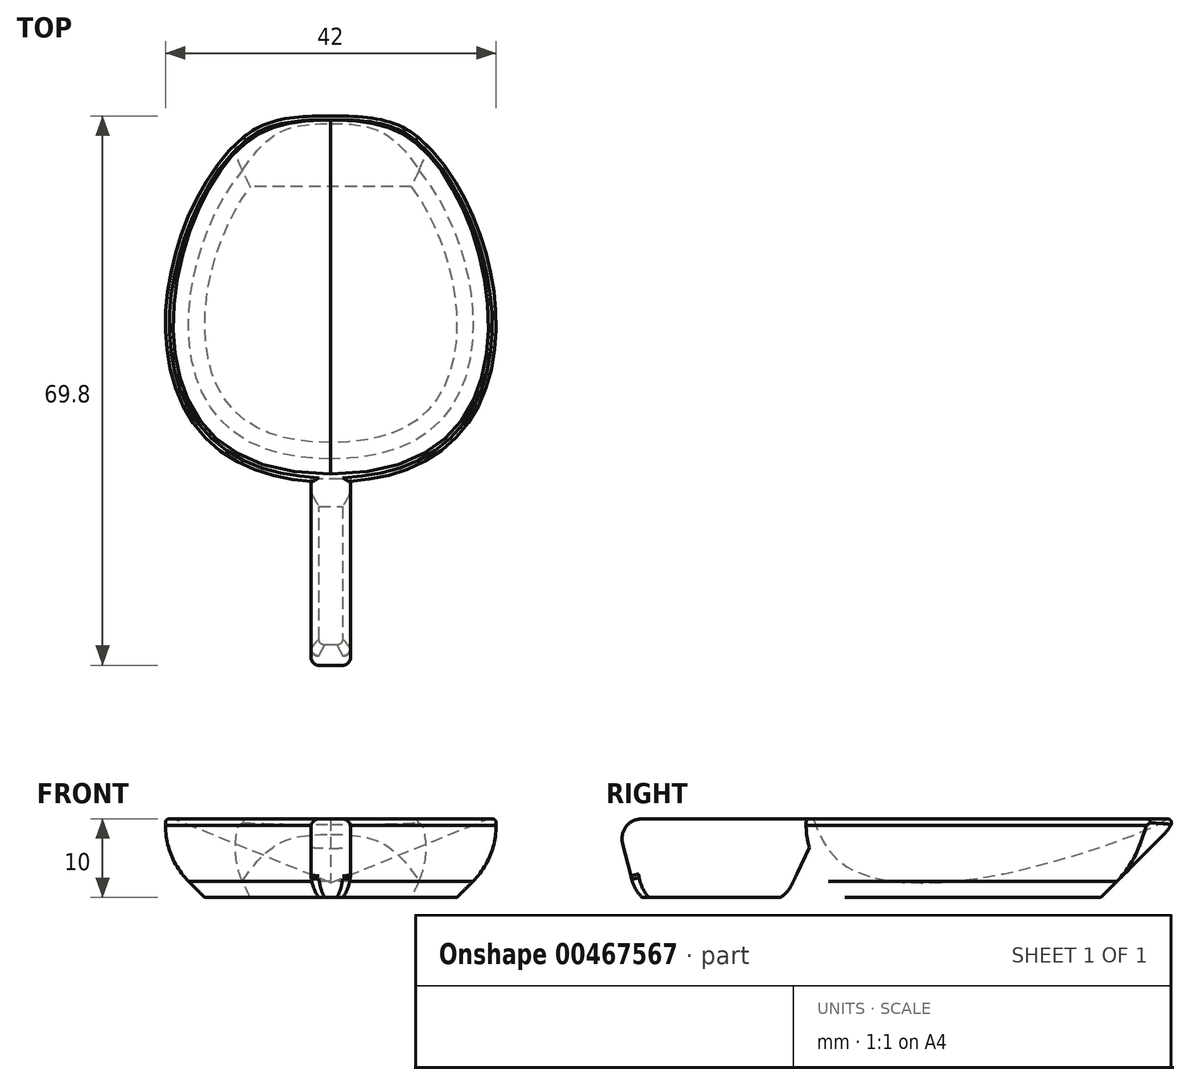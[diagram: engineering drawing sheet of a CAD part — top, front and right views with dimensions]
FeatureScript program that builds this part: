
annotation { "Feature Type Name" : "Feature", "Feature Type Description" : "" }
export const myFeature = defineFeature(function(context is Context, id is Id, definition is map)
    precondition{}
    {
        {
            var Q0;
            Q0=qCreatedBy(makeId("Top.planeOp"),FACE);
            var sketch = newSketch(context, id + "F0", { "sketchPlane" : qUnion([Q0])});
            skFitSpline(sketch, "E0", {"points": [v(0, 45) * mm, v(-12, 41) * mm, v(-20, 18) * mm, v(0, 0) * mm], "startDerivative": vector(-57.69, 0) * mm, "endDerivative": vector(118.66, 0) * mm});
            skLineSegment(sketch, "E1", {"start": v(0, 45) * mm, "end": v(0, 0) * mm});
            skSolve(sketch);
        }
        {
            var Q0;
            Q0=qCreatedBy(makeId("Right.planeOp"),FACE);
            var sketch = newSketch(context, id + "F1", { "sketchPlane" : qUnion([Q0])});
            skLineSegment(sketch, "E2", {"start": v(0, 0) * mm, "end": v(45, 0) * mm});
            skFitSpline(sketch, "E3", {"points": [v(0, 0) * mm, v(5, -6.5) * mm, v(24, -7) * mm, v(45, 0) * mm], "startDerivative": vector(12.5, -37.49) * mm, "endDerivative": vector(15.21, 11.4) * mm});
            skSolve(sketch);
        }
        {
            var Q0;
            Q0 = qSketchRegion(id + "F1", true);
            var Q1;
            Q1 = qSketchRegion(id + "F0", true);
            var Q2;
            Q2=sQuery(id+"FQMcYZS5QZvl0eC_1.wireOp",EDGE,"xzcCkyq8-KsDK-qB1P-N4Ot-IK7GxVPd1evt");
            loft(context, id + "F2", {"sheetProfilesArray" : [{ "sheetProfileEntities" : qUnion([Q0]) }, { "sheetProfileEntities" : qUnion([Q1]) }], "guidesArray" : [{ "guideEntities" : qUnion([Q2]), "guideDerivativeType" : LoftGuideDerivativeType.DEFAULT, "guideDerivativeMagnitude" : 1 }]});
        }
        {
            var Q0;
            Q0=makeQuery(id+"F2.opLoft","SWEPT_BODY",BODY,{"disambiguationData":[OSD([makeQuery(id+"F0.imprint","IMPRINT",FACE,{"disambiguationData":[TD([[makeQuery(id+"F0.imprint","IMPRINT",EDGE,{"derivedFrom":sQuery(id+"F0.wireOp",EDGE,"E0")}),1.0]])]}),makeQuery(id+"F1.imprint","IMPRINT",FACE,{"disambiguationData":[TD([[makeQuery(id+"F1.imprint","IMPRINT",EDGE,{"derivedFrom":sQuery(id+"F1.wireOp",EDGE,"C926cNkA-Lv8C-HaRY-GubS-DPcHZd8qW3n6")}),1.0]])]})])]});
            var Q1;
            Q1=qCreatedBy(makeId("Right.planeOp"),FACE);
            mirror(context, id + "F3", {"operationType" : NewBodyOperationType.ADD, "entities" : qUnion([Q0]), "mirrorPlane" : qUnion([Q1])});
        }
        {
            var Q0;
            Q0=qCreatedBy(makeId("Top.planeOp"),FACE);
            var sketch = newSketch(context, id + "F4", { "sketchPlane" : qUnion([Q0])});
            skFitSpline(sketch, "E4", {"points": [v(0, 46) * mm, v(-12, 42) * mm, v(-21, 19) * mm, v(0, -1) * mm], "startDerivative": vector(-58.67, 0) * mm, "endDerivative": vector(124, 0) * mm});
            skLineSegment(sketch, "E5", {"start": v(0, 46) * mm, "end": v(0, -1) * mm});
            skSolve(sketch);
        }
        {
            var Q0;
            Q0 = qSketchRegion(id + "F4", true);
            extrude(context, id + "F5", {"entities" : qUnion([Q0]), "oppositeDirection" : true, "depth" : 10 * mm});
        }
        {
            var Q0;
            Q0=makeQuery(id+"F2.opLoft","SWEPT_BODY",BODY,{"disambiguationData":[OSD([makeQuery(id+"F0.imprint","IMPRINT",FACE,{"disambiguationData":[TD([[makeQuery(id+"F0.imprint","IMPRINT",EDGE,{"derivedFrom":sQuery(id+"F0.wireOp",EDGE,"E0")}),1.0]])]}),makeQuery(id+"F1.imprint","IMPRINT",FACE,{"disambiguationData":[TD([[makeQuery(id+"F1.imprint","IMPRINT",EDGE,{"derivedFrom":sQuery(id+"F1.wireOp",EDGE,"C926cNkA-Lv8C-HaRY-GubS-DPcHZd8qW3n6")}),1.0]])]})])]});
            var Q1;
            Q1=makeQuery(id+"F5.opExtrude","SWEPT_BODY",BODY,{"disambiguationData":[OSD([sQuery(id+"F4.wireOp",EDGE,"E4"),sQuery(id+"F4.wireOp",EDGE,"E5")])]});
            booleanBodies(context, id + "F6", {"operationType" : BooleanOperationType.SUBTRACTION, "tools" : qUnion([Q0]), "targets" : qUnion([Q1])});
        }
        {
            var Q0;
            Q0=makeQuery(id+"F5.opExtrude","SWEPT_BODY",BODY,{"disambiguationData":[OSD([sQuery(id+"F4.wireOp",EDGE,"E4"),sQuery(id+"F4.wireOp",EDGE,"E5")])]});
            var Q1;
            Q1=qCreatedBy(makeId("Right.planeOp"),FACE);
            mirror(context, id + "F7", {"operationType" : NewBodyOperationType.ADD, "entities" : qUnion([Q0]), "mirrorPlane" : qUnion([Q1])});
        }
        {
            var Q0;
            Q0=qCreatedBy(makeId("Right.planeOp"),FACE);
            var sketch = newSketch(context, id + "F8", { "sketchPlane" : qUnion([Q0])});
            skLineSegment(sketch, "E6", {"start": v(0, 0) * mm, "end": v(-25, 0) * mm});
            skLineSegment(sketch, "E7", {"start": v(-25, 0) * mm, "end": v(-22.5, -10) * mm});
            skLineSegment(sketch, "E8", {"start": v(-22.5, -10) * mm, "end": v(-3.5, -10) * mm});
            skLineSegment(sketch, "E9", {"start": v(-3.5, -10) * mm, "end": v(0, -2.5) * mm});
            skLineSegment(sketch, "E10", {"start": v(0, -2.5) * mm, "end": v(0, -2.5) * mm});
            skLineSegment(sketch, "E11", {"start": v(0, -2.5) * mm, "end": v(0, 0) * mm});
            skSolve(sketch);
        }
        {
            var Q0;
            Q0 = qSketchRegion(id + "F8", true);
            extrude(context, id + "F9", {"entities" : qUnion([Q0]), "operationType" : NewBodyOperationType.ADD, "endBound" : BoundingType.SYMMETRIC, "depth" : 5 * mm});
        }
        {
            var Q0;
            Q0=qCreatedBy(makeId("Right.planeOp"),FACE);
            var sketch = newSketch(context, id + "F10", { "sketchPlane" : qUnion([Q0])});
            skLineSegment(sketch, "E12", {"start": v(46.5, 0) * mm, "end": v(31.5, -15) * mm});
            skLineSegment(sketch, "E13", {"start": v(31.5, -15) * mm, "end": v(46.5, -15) * mm});
            skLineSegment(sketch, "E14", {"start": v(46.5, -15) * mm, "end": v(46.5, 0) * mm});
            skSolve(sketch);
        }
        {
            var Q0;
            Q0 = qSketchRegion(id + "F10", true);
            extrude(context, id + "F11", {"entities" : qUnion([Q0]), "operationType" : NewBodyOperationType.REMOVE, "endBound" : BoundingType.SYMMETRIC, "depth" : 25 * mm});
        }
        {
            var Q0;
            Q0=makeQuery(id+"F11.boolean.opBoolean","INTERSECT",EDGE,{"derivedFrom":[makeQuery(id+"F5.opExtrude","SWEPT_FACE",FACE,{"disambiguationData":[OSD([sQuery(id+"F4.wireOp",EDGE,"E4")])]}),makeQuery(id+"F11.opExtrude","SWEPT_FACE",FACE,{"disambiguationData":[OSD([sQuery(id+"F10.wireOp",EDGE,"E12")])]})]});
            var Q1;
            Q1=makeQuery(id+"F11.boolean.opBoolean","INTERSECT",EDGE,{"derivedFrom":[makeQuery(id+"F7.opPattern","COPY",FACE,{"derivedFrom":makeQuery(id+"F5.opExtrude","SWEPT_FACE",FACE,{"disambiguationData":[OSD([sQuery(id+"F4.wireOp",EDGE,"E4")])]}),"instanceName":"1"}),makeQuery(id+"F11.opExtrude","SWEPT_FACE",FACE,{"disambiguationData":[OSD([sQuery(id+"F10.wireOp",EDGE,"E12")])]})]});
            fillet(context, id + "F12", {"entities" : qUnion([Q0, Q1]), "radius" : 5 * mm, "tangentPropagation" : true, "allowEdgeOverflow" : false});
        }
        {
            var Q0;
            Q0=makeQuery(id+"F7.opPattern","COPY",EDGE,{"derivedFrom":makeQuery(id+"F5.opExtrude","CAP_EDGE",EDGE,{"disambiguationData":[OSD([sQuery(id+"F4.wireOp",EDGE,"E4")])],"isStart":false}),"instanceName":"1"});
            chamfer(context, id + "F13", {"entities" : qUnion([Q0]), "width" : 5 * mm, "tangentPropagation" : true});
        }
        {
            var Q0;
            Q0=makeQuery(id+"F9.opExtrude","SWEPT_FACE",FACE,{"disambiguationData":[OSD([sQuery(id+"F8.wireOp",EDGE,"E8")])]});
            chamfer(context, id + "F14", {"entities" : qUnion([Q0]), "width" : 1 * mm, "tangentPropagation" : true});
        }
        {
            var Q0;
            {var subQ0=sQuery(id+"F8.wireOp",EDGE,"E9");Q0=makeQuery(id+"F14.opChamfer","BLEND_EDGE",EDGE,{"blendedFrom":[makeQuery(id+"F9.opExtrude","SWEPT_EDGE",EDGE,{"disambiguationData":[OSD([sQuery(id+"F8.wireOp",EDGE,"E8"),subQ0])]}),makeQuery(id+"F9.opExtrude","SWEPT_FACE",FACE,{"disambiguationData":[OSD([subQ0])]})],"blendedInto":[makeQuery(id+"F9.opExtrude","SWEPT_FACE",FACE,{"disambiguationData":[OSD([subQ0])]})]});}
            var Q1;
            {var subQ0=sQuery(id+"F8.wireOp",EDGE,"E8");Q1=makeQuery(id+"F14.opChamfer","BLEND_EDGE",EDGE,{"blendedFrom":[makeQuery(id+"F9.opExtrude","CAP_EDGE",EDGE,{"disambiguationData":[OSD([subQ0])],"isStart":true}),makeQuery(id+"F9.opExtrude","CAP_FACE",FACE,{"disambiguationData":[OSD([sQuery(id+"F8.wireOp",EDGE,"E6"),sQuery(id+"F8.wireOp",EDGE,"E7"),subQ0,sQuery(id+"F8.wireOp",EDGE,"E9"),sQuery(id+"F8.wireOp",EDGE,"E11")])],"isStart":true})],"blendedInto":[makeQuery(id+"F9.opExtrude","CAP_FACE",FACE,{"disambiguationData":[OSD([sQuery(id+"F8.wireOp",EDGE,"E6"),sQuery(id+"F8.wireOp",EDGE,"E7"),subQ0,sQuery(id+"F8.wireOp",EDGE,"E9"),sQuery(id+"F8.wireOp",EDGE,"E11")])],"isStart":true})]});}
            var Q2;
            {var subQ0=sQuery(id+"F8.wireOp",EDGE,"E7");Q2=makeQuery(id+"F14.opChamfer","BLEND_EDGE",EDGE,{"blendedFrom":[makeQuery(id+"F9.opExtrude","SWEPT_EDGE",EDGE,{"disambiguationData":[OSD([subQ0,sQuery(id+"F8.wireOp",EDGE,"E8")])]}),makeQuery(id+"F9.opExtrude","SWEPT_FACE",FACE,{"disambiguationData":[OSD([subQ0])]})],"blendedInto":[makeQuery(id+"F9.opExtrude","SWEPT_FACE",FACE,{"disambiguationData":[OSD([subQ0])]})]});}
            var Q3;
            {var subQ0=sQuery(id+"F8.wireOp",EDGE,"E8");Q3=makeQuery(id+"F14.opChamfer","BLEND_EDGE",EDGE,{"blendedFrom":[makeQuery(id+"F9.opExtrude","CAP_EDGE",EDGE,{"disambiguationData":[OSD([subQ0])],"isStart":false}),makeQuery(id+"F9.opExtrude","CAP_FACE",FACE,{"disambiguationData":[OSD([sQuery(id+"F8.wireOp",EDGE,"E6"),sQuery(id+"F8.wireOp",EDGE,"E7"),subQ0,sQuery(id+"F8.wireOp",EDGE,"E9"),sQuery(id+"F8.wireOp",EDGE,"E11")])],"isStart":false})],"blendedInto":[makeQuery(id+"F9.opExtrude","CAP_FACE",FACE,{"disambiguationData":[OSD([sQuery(id+"F8.wireOp",EDGE,"E6"),sQuery(id+"F8.wireOp",EDGE,"E7"),subQ0,sQuery(id+"F8.wireOp",EDGE,"E9"),sQuery(id+"F8.wireOp",EDGE,"E11")])],"isStart":false})]});}
            fillet(context, id + "F15", {"entities" : qUnion([Q0, Q1, Q2, Q3]), "radius" : 5 * mm, "tangentPropagation" : true, "allowEdgeOverflow" : false});
        }
        {
            var Q0;
            Q0=makeQuery(id+"F9.opExtrude","SWEPT_EDGE",EDGE,{"disambiguationData":[OSD([sQuery(id+"F8.wireOp",EDGE,"E6"),sQuery(id+"F8.wireOp",EDGE,"E7")])]});
            fillet(context, id + "F16", {"entities" : qUnion([Q0]), "radius" : 2.5 * mm, "tangentPropagation" : true, "allowEdgeOverflow" : false});
        }
        {
            var Q0;
            Q0=makeQuery(id+"F9.opExtrude","CAP_EDGE",EDGE,{"disambiguationData":[OSD([sQuery(id+"F8.wireOp",EDGE,"E6")])],"isStart":true});
            var Q1;
            Q1=makeQuery(id+"F9.opExtrude","CAP_EDGE",EDGE,{"disambiguationData":[OSD([sQuery(id+"F8.wireOp",EDGE,"E6")])],"isStart":false});
            fillet(context, id + "F17", {"entities" : qUnion([Q0, Q1]), "radius" : 1 * mm, "tangentPropagation" : true, "allowEdgeOverflow" : false});
        }
        {
            var Q0;
            Q0=makeQuery(id+"F5.opExtrude","CAP_EDGE",EDGE,{"disambiguationData":[OSD([sQuery(id+"F4.wireOp",EDGE,"E4")])],"isStart":true});
            var Q1;
            Q1=makeQuery(id+"F6.opBoolean","COPY",EDGE,{"derivedFrom":makeQuery(id+"F2.opLoft","MID_CAP_EDGE",EDGE,{"disambiguationData":[OSD([sQuery(id+"F0.wireOp",EDGE,"E0"),sQuery(id+"F0.wireOp",EDGE,"E1")])],"capPos":1.0})});
            fillet(context, id + "F18", {"entities" : qUnion([Q0, Q1]), "radius" : 0.5 * mm, "tangentPropagation" : true, "allowEdgeOverflow" : false});
        }
        {
            var Q0;
            {var subQ0=sQuery(id+"F4.wireOp",EDGE,"E4");Q0=makeQuery(id+"F13.opChamfer","BLEND_EDGE",EDGE,{"blendedFrom":[makeQuery(id+"F7.opPattern","COPY",EDGE,{"derivedFrom":makeQuery(id+"F5.opExtrude","CAP_EDGE",EDGE,{"disambiguationData":[OSD([subQ0])],"isStart":false}),"instanceName":"1"}),makeQuery(id+"F7.opPattern","COPY",FACE,{"derivedFrom":makeQuery(id+"F5.opExtrude","SWEPT_FACE",FACE,{"disambiguationData":[OSD([subQ0])]}),"instanceName":"1"})],"blendedInto":[makeQuery(id+"F7.opPattern","COPY",FACE,{"derivedFrom":makeQuery(id+"F5.opExtrude","SWEPT_FACE",FACE,{"disambiguationData":[OSD([subQ0])]}),"instanceName":"1"})]});}
            fillet(context, id + "F19", {"entities" : qUnion([Q0]), "radius" : 10 * mm, "tangentPropagation" : true, "allowEdgeOverflow" : false});
        }
    });
